# Revit family: VL2S-LEN-DI152xWS840Bx
name_source: partatom
category: Leuchten
units: mm (PartAtom-declared; Revit-internal decimal feet)

## family parameters
Basisbauteil = Fläche
Beim Laden mit Abzugskörper schneiden = Nein
Bemaßung runder Anschluss = Durchmesser verwenden
Gemeinsam genutzt = Nein
Lichtquelle = Ja
OmniClass-Nummer = 23.80.70.11
OmniClass-Titel = Luminaries for Internal Lighting
Raumberechnungspunkt = Nein
Teiletyp = Normal

## types (2) — shared parameters
Baugruppenkennzeichen = D5020200
Datei für fotometrisches Netz = V-LENSES-DI.IES
Emissionsform beim Rendern sichtbar = Nein
Farbfilter = 16777215
Farbtemperaturverschiebung bei Dämpfen der Lampe = <Keine Auswahl>
Hersteller = RIDI Leuchten GmbH
Lampe = LED
Neigungswinkel = 90.00°
URL = www.ridi.de
Von Breite des Rechtecks ausssenden = 1525 mm  [stored 5.00328 ft]
Von Länge des Rechtecks aussenden = 112 mm  [stored 0.367454 ft]
brand = RIDI
conformity mark = CE
electrical safety class = 1
height = 86 mm  [stored 0.282152 ft]
ingress protection (IP) code = IP20
length = 1528 mm  [stored 5.01312 ft]
nominal frequency = 50-60Hz
nominal voltage = 230
voltage type (AC, DC, UC) = AC
weight = 4,05kg
width = 113 mm  [stored 0.370735 ft]
zero-valued in all types: Vorgabe-Ansicht

## per-type parameters (varying)
| type | Modell | Scheinlast | rated input power |
| VL2S-LEN-DI152-5FLWS840B0850 | 2550003 | 56 VA | 56 |
| VL2S-LEN-DI152-7DAWS840B0750 | 2560003 | 48 VA | 48 |

note: column(s) folded — value = type name in every type: product name

note: [stored X ft] marks values corroborated as IEEE doubles in the binary element streams (Revit-internal decimal feet)
